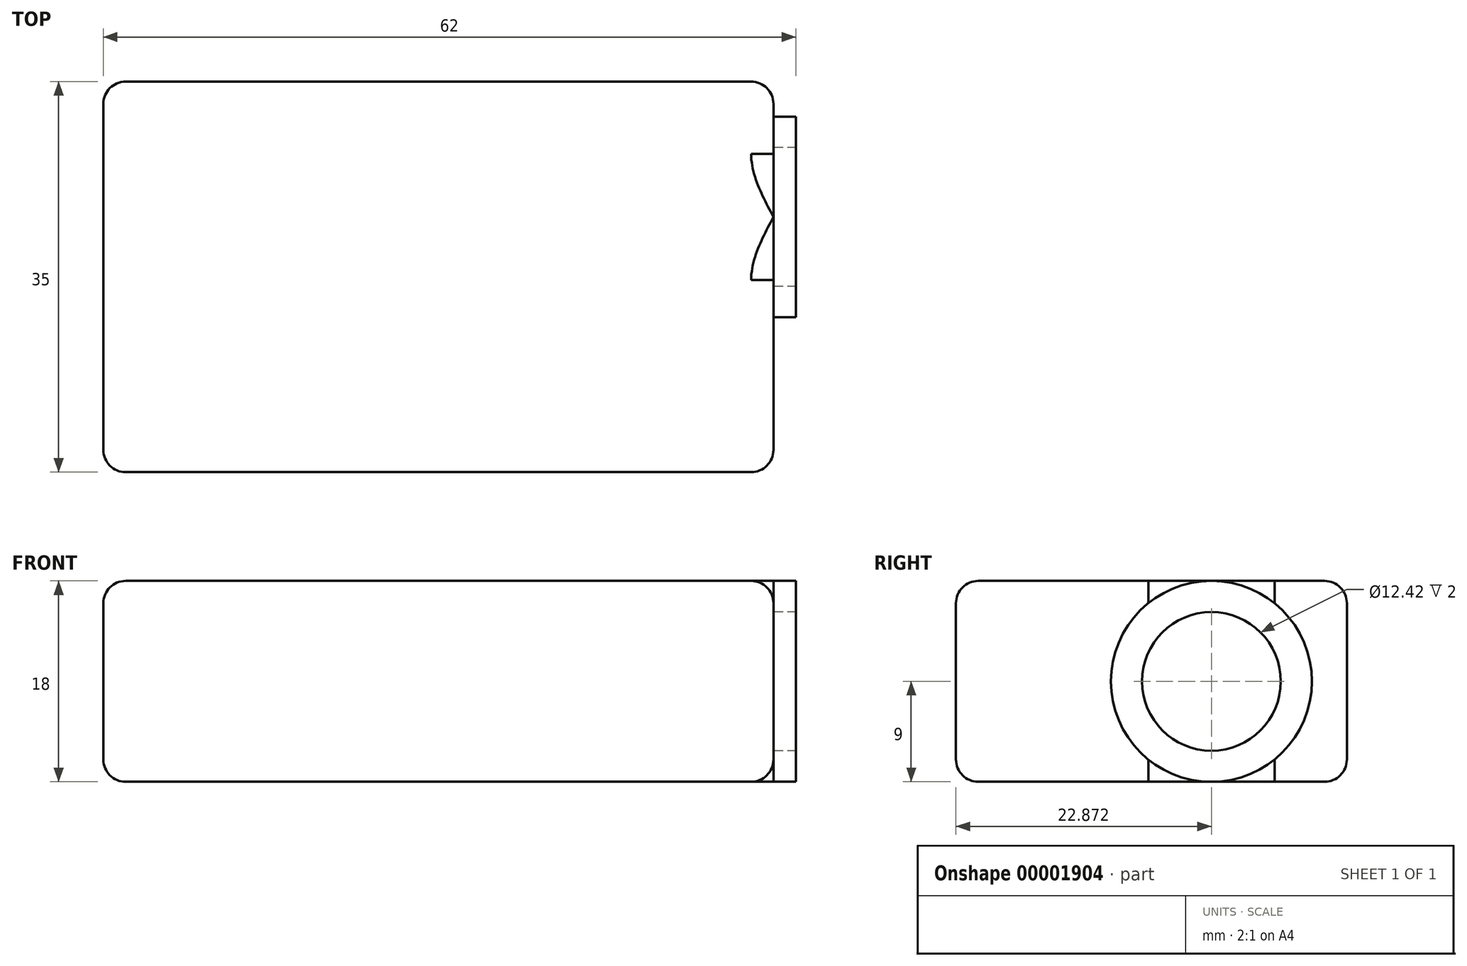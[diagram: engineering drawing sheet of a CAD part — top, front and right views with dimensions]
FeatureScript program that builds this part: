
annotation { "Feature Type Name" : "Feature", "Feature Type Description" : "" }
export const myFeature = defineFeature(function(context is Context, id is Id, definition is map)
    precondition{}
    {
        {
            var Q0;
            Q0=qCreatedBy(makeId("Right.planeOp"),FACE);
            var sketch = newSketch(context, id + "F0", { "sketchPlane" : qUnion([Q0])});
            skLineSegment(sketch, "E0.rect.bottom", {"start": v(17.5, -9) * mm, "end": v(-17.5, -9) * mm});
            skLineSegment(sketch, "E0.rect.top", {"start": v(17.5, 9) * mm, "end": v(-17.5, 9) * mm});
            skLineSegment(sketch, "E0.rect.left", {"start": v(17.5, -9) * mm, "end": v(17.5, 9) * mm});
            skLineSegment(sketch, "E0.rect.right", {"start": v(-17.5, -9) * mm, "end": v(-17.5, 9) * mm});
            skPoint(sketch, "E0.rect.middle", {"position": v(0, 0) * mm});
            skSolve(sketch);
        }
        {
            var Q0;
            Q0=makeQuery(id+"F0.imprint","IMPRINT",FACE,{"disambiguationData":[TD([[makeQuery(id+"F0.imprint","IMPRINT",EDGE,{"derivedFrom":sQuery(id+"F0.wireOp",EDGE,"E0.rect.bottom")}),-1.0]])]});
            extrude(context, id + "F1", {"entities" : qUnion([Q0]), "oppositeDirection" : true, "depth" : 60 * mm});
        }
        {
            var Q0;
            Q0=qCreatedBy(makeId("Right.planeOp"),FACE);
            var sketch = newSketch(context, id + "F2", { "sketchPlane" : qUnion([Q0])});
            skCircle(sketch, "E1", {"center": v(5.37, 0) * mm, "radius": 9 * mm});
            skCircle(sketch, "E2", {"center": v(5.37, 0) * mm, "radius": 6.21 * mm});
            skSolve(sketch);
        }
        {
            var Q0;
            Q0=makeQuery(id+"F2.imprint","IMPRINT",FACE,{"disambiguationData":[TD([[makeQuery(id+"F2.imprint","IMPRINT",EDGE,{"derivedFrom":sQuery(id+"F2.wireOp",EDGE,"E1")}),1.0]])]});
            extrude(context, id + "F3", {"entities" : qUnion([Q0]), "operationType" : NewBodyOperationType.ADD, "depth" : 2 * mm});
        }
        {
            var Q0;
            Q0=makeQuery(id+"F1.opExtrude","SWEPT_FACE",FACE,{"disambiguationData":[OSD([sQuery(id+"F0.wireOp",EDGE,"E0.rect.top")])]});
            var Q1;
            Q1=makeQuery(id+"F1.opExtrude","CAP_FACE",FACE,{"disambiguationData":[OSD([sQuery(id+"F0.wireOp",EDGE,"E0.rect.bottom"),sQuery(id+"F0.wireOp",EDGE,"E0.rect.top"),sQuery(id+"F0.wireOp",EDGE,"E0.rect.left"),sQuery(id+"F0.wireOp",EDGE,"E0.rect.right")])],"isStart":false});
            var Q2;
            Q2=makeQuery(id+"F1.opExtrude","SWEPT_EDGE",EDGE,{"disambiguationData":[OSD([sQuery(id+"F0.wireOp",EDGE,"E0.rect.bottom"),sQuery(id+"F0.wireOp",EDGE,"E0.rect.left")])]});
            var Q3;
            Q3=makeQuery(id+"F1.opExtrude","SWEPT_FACE",FACE,{"disambiguationData":[OSD([sQuery(id+"F0.wireOp",EDGE,"E0.rect.right")])]});
            var Q4;
            Q4=makeQuery(id+"F1.opExtrude","SWEPT_FACE",FACE,{"disambiguationData":[OSD([sQuery(id+"F0.wireOp",EDGE,"E0.rect.bottom")])]});
            var Q5;
            Q5=makeQuery(id+"F1.opExtrude","CAP_EDGE",EDGE,{"disambiguationData":[OSD([sQuery(id+"F0.wireOp",EDGE,"E0.rect.left")])],"isStart":true});
            fillet(context, id + "F4", {"entities" : qUnion([Q0, Q1, Q2, Q3, Q4, Q5]), "radius" : 2 * mm, "tangentPropagation" : true, "allowEdgeOverflow" : false});
        }
    });
